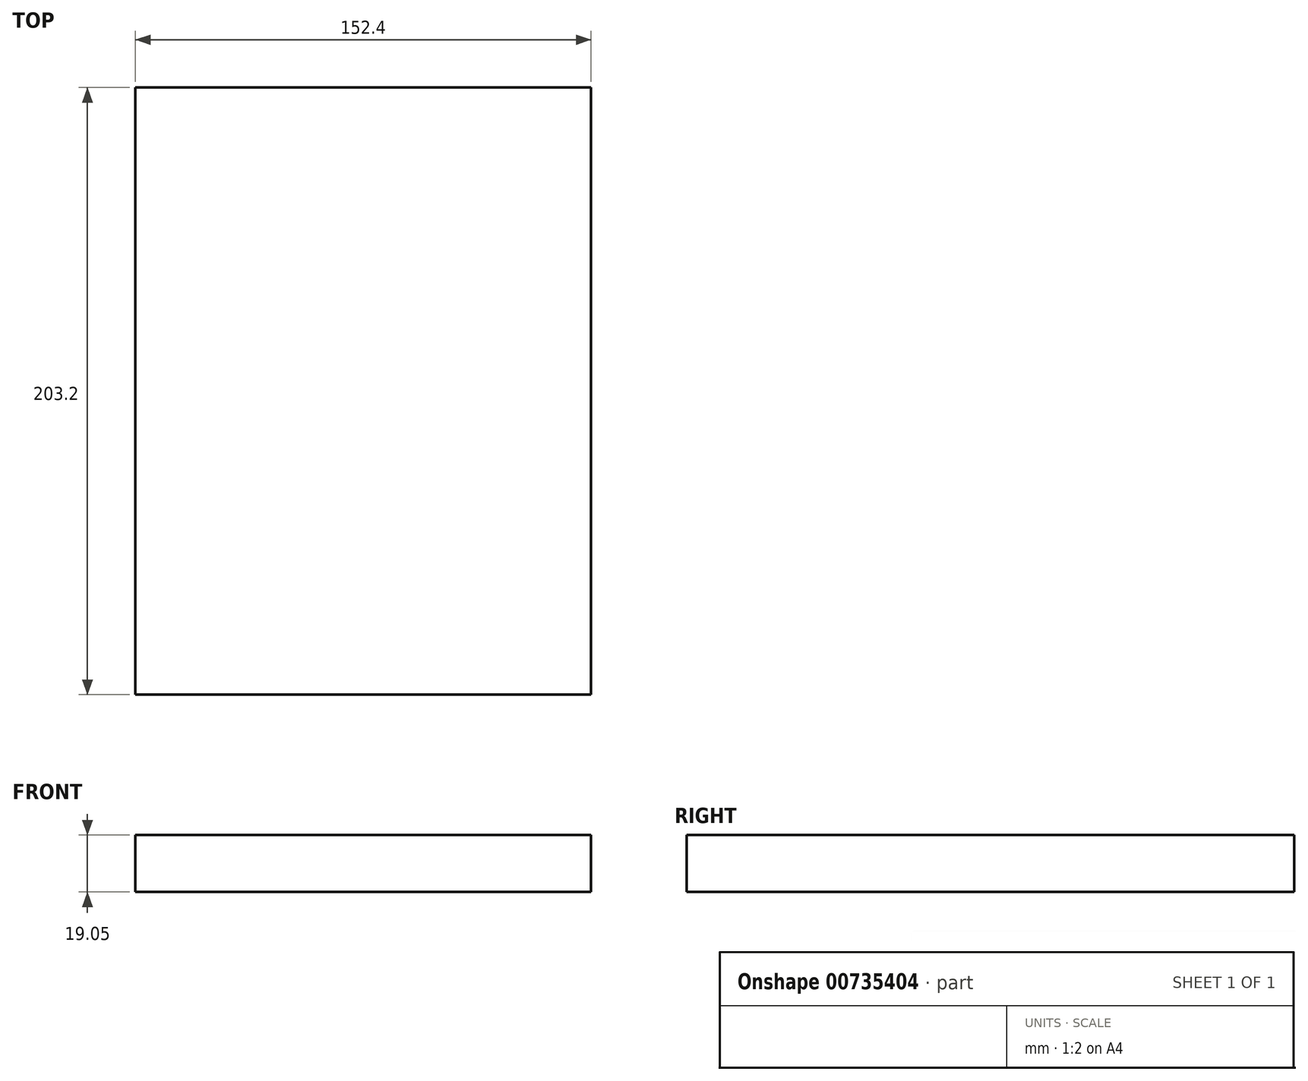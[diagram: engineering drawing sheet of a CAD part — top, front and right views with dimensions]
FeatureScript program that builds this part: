
annotation { "Feature Type Name" : "Feature", "Feature Type Description" : "" }
export const myFeature = defineFeature(function(context is Context, id is Id, definition is map)
    precondition{}
    {
        {
            var Q0;
            Q0=qCreatedBy(makeId("Top.planeOp"),FACE);
            var sketch = newSketch(context, id + "F0", { "sketchPlane" : qUnion([Q0])});
            skLineSegment(sketch, "E0.bottom", {"start": v(-96.66, 102.21) * mm, "end": v(55.74, 102.21) * mm});
            skLineSegment(sketch, "E0.top", {"start": v(-96.66, -100.99) * mm, "end": v(55.74, -100.99) * mm});
            skLineSegment(sketch, "E0.left", {"start": v(-96.66, 102.21) * mm, "end": v(-96.66, -100.99) * mm});
            skLineSegment(sketch, "E0.right", {"start": v(55.74, 102.21) * mm, "end": v(55.74, -100.99) * mm});
            skSolve(sketch);
        }
        {
            var Q0;
            Q0=makeQuery(id+"F0.imprint","IMPRINT",FACE,{"disambiguationData":[TD([[makeQuery(id+"F0.imprint","IMPRINT",EDGE,{"derivedFrom":sQuery(id+"F0.wireOp",EDGE,"E0.bottom")}),-1.0]])]});
            extrude(context, id + "F1", {"entities" : qUnion([Q0]), "depth" : 19.05 * mm, "offsetDistance" : 25.4 * mm});
        }
    });
